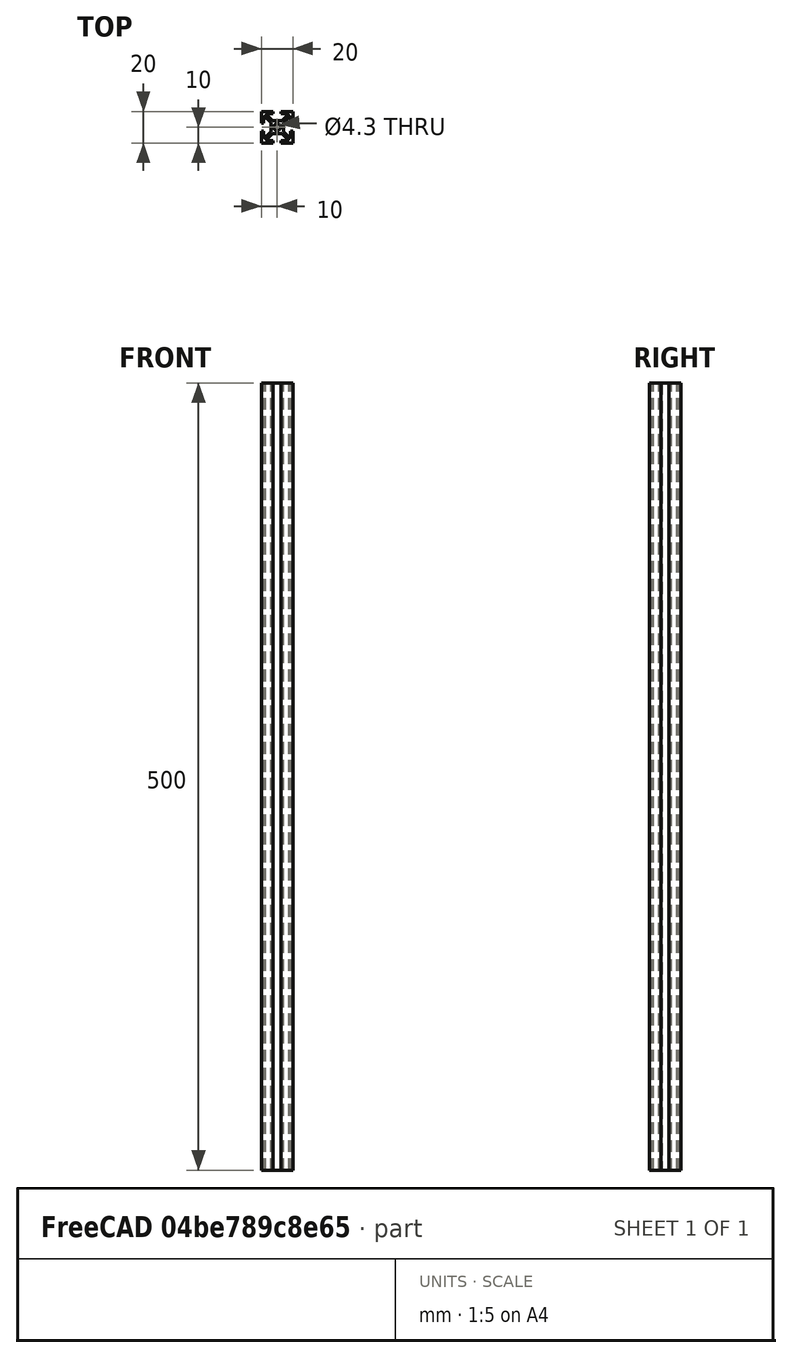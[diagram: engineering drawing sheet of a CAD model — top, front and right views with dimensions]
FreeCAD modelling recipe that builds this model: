
FCSTD DOCUMENT  (FreeCAD 0.16R6706 (Git))
Label: 20x20_extruded_aluminum
License: All rights reserved
LicenseURL: http://en.wikipedia.org/wiki/All_rights_reserved
objects: Sketcher::SketchObject×1, PartDesign::Pad×1
note: 3 computed .brp shape members not serialized (recipe doc carries the construction recipe); baked Part::Feature solids carry a one-line shape summary decoded from their .brp

FEATURE [Sketcher::SketchObject] Sketch
  sketch-geometry (37):
    g0: LineSegment StartX=-4 StartY=2.93934 StartZ=0 EndX=-4 EndY=-2.93934 EndZ=0
    g1: LineSegment StartX=-4 StartY=-2.93934 StartZ=0 EndX=-8.5 EndY=-7.43934 EndZ=0
    g2: LineSegment StartX=-8.5 StartY=-7.43934 StartZ=0 EndX=-8.5 EndY=-2.5 EndZ=0
    g3: LineSegment StartX=-8.5 StartY=-2.5 StartZ=0 EndX=-10 EndY=-2.5 EndZ=0
    g4: LineSegment StartX=-10 StartY=-2.5 StartZ=0 EndX=-10 EndY=-10 EndZ=0
    g5: LineSegment StartX=-10 StartY=-10 StartZ=0 EndX=-2.5 EndY=-10 EndZ=0
    g6: LineSegment StartX=-2.5 StartY=-10 StartZ=0 EndX=-2.5 EndY=-8.5 EndZ=0
    g7: LineSegment StartX=-2.5 StartY=-8.5 StartZ=0 EndX=-7.43934 EndY=-8.5 EndZ=0
    g8: LineSegment StartX=-7.43934 StartY=-8.5 StartZ=0 EndX=-2.93934 EndY=-4 EndZ=0
    g9: LineSegment StartX=-2.93934 StartY=-4 StartZ=0 EndX=2.93934 EndY=-4 EndZ=0
    g10: LineSegment StartX=2.93934 StartY=-4 StartZ=0 EndX=7.43933 EndY=-8.5 EndZ=0
    g11: LineSegment StartX=7.43933 StartY=-8.5 StartZ=0 EndX=2.5 EndY=-8.5 EndZ=0
    g12: LineSegment StartX=2.5 StartY=-8.5 StartZ=0 EndX=2.5 EndY=-10 EndZ=0
    g13: LineSegment StartX=2.5 StartY=-10 StartZ=0 EndX=10 EndY=-10 EndZ=0
    g14: LineSegment StartX=10 StartY=-10 StartZ=0 EndX=10 EndY=-2.5 EndZ=0
    g15: LineSegment StartX=10 StartY=-2.5 StartZ=0 EndX=8.5 EndY=-2.5 EndZ=0
    g16: LineSegment StartX=8.5 StartY=-2.5 StartZ=0 EndX=8.5 EndY=-7.43935 EndZ=0
    g17: LineSegment StartX=8.5 StartY=-7.43935 StartZ=0 EndX=4 EndY=-2.93934 EndZ=0
    g18: LineSegment StartX=4 StartY=-2.93934 StartZ=0 EndX=4 EndY=2.93934 EndZ=0
    g19: LineSegment StartX=4 StartY=2.93934 StartZ=0 EndX=8.5 EndY=7.43933 EndZ=0
    g20: LineSegment StartX=8.5 StartY=7.43933 StartZ=0 EndX=8.5 EndY=2.5 EndZ=0
    g21: LineSegment StartX=8.5 StartY=2.5 StartZ=0 EndX=10 EndY=2.5 EndZ=0
    g22: LineSegment StartX=10 StartY=2.5 StartZ=0 EndX=10 EndY=10 EndZ=0
    g23: LineSegment StartX=10 StartY=10 StartZ=0 EndX=2.5 EndY=10 EndZ=0
    g24: LineSegment StartX=2.5 StartY=10 StartZ=0 EndX=2.5 EndY=8.5 EndZ=0
    g25: LineSegment StartX=2.5 StartY=8.5 StartZ=0 EndX=7.43935 EndY=8.5 EndZ=0
    g26: LineSegment StartX=7.43935 StartY=8.5 StartZ=0 EndX=2.93934 EndY=4 EndZ=0
    g27: LineSegment StartX=2.93934 StartY=4 StartZ=0 EndX=-2.93934 EndY=4 EndZ=0
    g28: LineSegment StartX=-2.93934 StartY=4 StartZ=0 EndX=-7.43935 EndY=8.5 EndZ=0
    g29: LineSegment StartX=-7.43935 StartY=8.5 StartZ=0 EndX=-2.5 EndY=8.5 EndZ=0
    g30: LineSegment StartX=-2.5 StartY=8.5 StartZ=0 EndX=-2.5 EndY=10 EndZ=0
    g31: LineSegment StartX=-2.5 StartY=10 StartZ=0 EndX=-10 EndY=10 EndZ=0
    g32: LineSegment StartX=-10 StartY=10 StartZ=0 EndX=-10 EndY=2.5 EndZ=0
    g33: LineSegment StartX=-10 StartY=2.5 StartZ=0 EndX=-8.5 EndY=2.5 EndZ=0
    g34: LineSegment StartX=-8.5 StartY=2.5 StartZ=0 EndX=-8.5 EndY=7.43933 EndZ=0
    g35: LineSegment StartX=-8.5 StartY=7.43933 StartZ=0 EndX=-4 EndY=2.93934 EndZ=0
    g36: Circle CenterX=0 CenterY=0 CenterZ=0 NormalX=0 NormalY=0 NormalZ=1 Radius=2.15
  constraints (110):
    c: Coincident(g0,g1)
    c: Coincident(g1,g2)
    c: Coincident(g2,g3)
    c: Coincident(g3,g4)
    c: Coincident(g4,g5)
    c: Coincident(g5,g6)
    c: Coincident(g6,g7)
    c: Coincident(g7,g8)
    c: Coincident(g8,g9)
    c: Coincident(g9,g10)
    c: Coincident(g10,g11)
    c: Coincident(g11,g12)
    c: Coincident(g12,g13)
    c: Coincident(g13,g14)
    c: Coincident(g15,g16)
    c: Coincident(g16,g17)
    c: Coincident(g17,g18)
    c: Coincident(g18,g19)
    c: Coincident(g19,g20)
    c: Coincident(g20,g21)
    c: Coincident(g21,g22)
    c: Coincident(g22,g23)
    c: Coincident(g23,g24)
    c: Coincident(g24,g25)
    c: Coincident(g25,g26)
    c: Coincident(g27,g28)
    c: Coincident(g28,g29)
    c: Coincident(g29,g30)
    c: Coincident(g30,g31)
    c: Coincident(g31,g32)
    c: Coincident(g32,g33)
    c: Coincident(g33,g34)
    c: Coincident(g34,g35)
    c: Coincident(g35,g0)
    c: Horizontal(g27)
    c: Horizontal(g9)
    c: Vertical(g0)
    c: Vertical(g18)
    c: Vertical(g22)
    c: Vertical(g20)
    c: Vertical(g34)
    c: Horizontal(g31)
    c: Vertical(g2)
    c: Horizontal(g7)
    c: Vertical(g6)
    c: Horizontal(g13)
    c: Vertical(g12)
    c: Horizontal(g11)
    c: Vertical(g14)
    c: Horizontal(g15)
    c: Vertical(g16)
    c: Horizontal(g21)
    c: Distance(g26,g18) = 1.5
    c: Distance(g17,g9) = 1.5
    c: Distance(g8,g0) = 1.5
    c: Distance(g27,g0) = 1.5
    c: Distance(g25,g19) = 1.5
    c: Distance(g28,g34) = 1.5
    c: Distance(g1,g7) = 1.5
    c: Distance(g16,g10) = 1.5
    c: DistanceY(g12,g12) = 1.5
    c: DistanceX(g15,g15) = 1.5
    c: Coincident(g14,g15)
    c: DistanceX(g21,g21) = 1.5
    c: Horizontal(g25)
    c: DistanceY(g24,g24) = 1.5
    c: Horizontal(g23)
    c: Horizontal(g29)
    c: DistanceY(g30,g30) = 1.5
    c: DistanceX(g33,g33) = 1.5
    c: Vertical(g32)
    c: DistanceX(g3,g3) = 1.5
    c: DistanceY(g6,g6) = 1.5
    c: Horizontal(g5)
    c: Vertical(g4)
    c: Vertical(g30)
    c: Horizontal(g33)
    c: DistanceX(g31,g31) = 7.5
    c: DistanceY(g32,g32) = 7.5
    c: DistanceX(g23,g23) = 7.5
    c: Vertical(g24)
    c: DistanceY(g22,g22) = 7.5
    c: DistanceY(g14,g14) = 7.5
    c: DistanceX(g13,g13) = 7.5
    c: DistanceX(g5,g5) = 7.5
    c: DistanceY(g4,g4) = 7.5
    c: Horizontal(g3)
    c: Distance(g30,g23) = 5
    c: Coincident(g26,g27)
    c: Parallel(g35,g28)
    c: Parallel(g19,g26)
    c: Parallel(g17,g10)
    c: Parallel(g8,g1)
    c: DistanceY(g-1,g22) = 10
    c: DistanceX(g-2,g22) = 10
    c: DistanceX(g-2,g31) = -10
    c: DistanceY(g-1,g4) = -10
    c: DistanceX(g-2,g4) = -10
    c: DistanceY(g-1,g13) = -10
    c: DistanceX(g-2,g13) = 10
    c: DistanceX(g0,g18) = 8
    c: DistanceY(g8,g27) = 8
    c: DistanceY(g-1,g27) = 4
    c: DistanceX(g-2,g18) = 4
    c: Symmetric(g9,g8,g-2)
    c: Equal(g0,g9)
    c: Equal(g9,g18)
    c: Equal(g18,g27)
    c: Radius(g36) = 2.15
    c: Coincident(g36,g-1)
FEATURE [PartDesign::Pad] Pad
  Length = 500
  Length2 = 100
  Sketch = -> Sketch
  Type = 0
